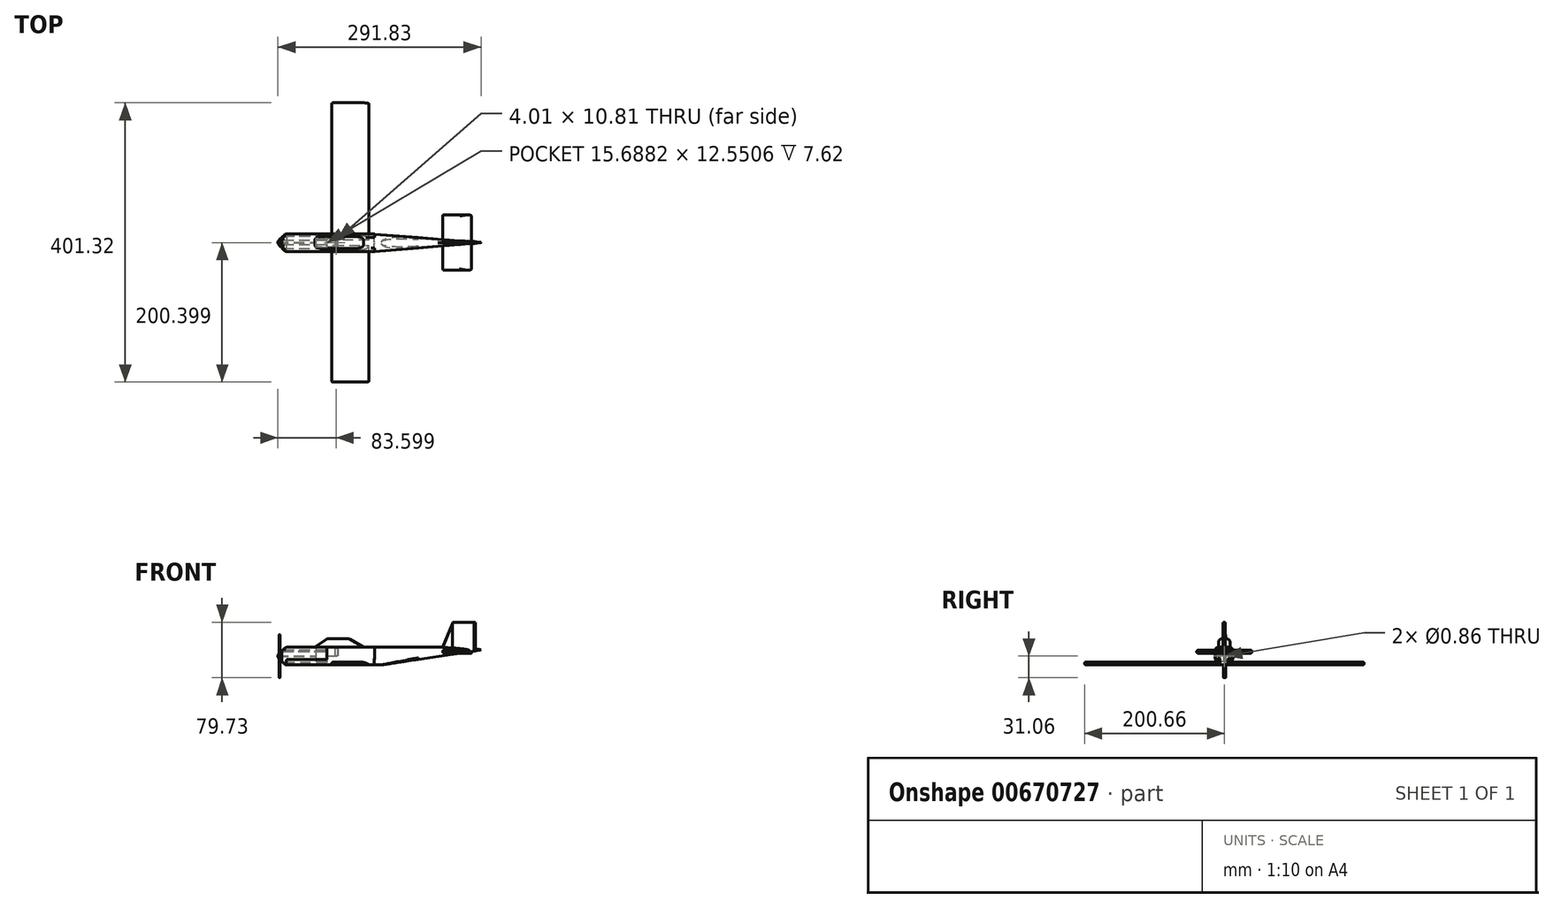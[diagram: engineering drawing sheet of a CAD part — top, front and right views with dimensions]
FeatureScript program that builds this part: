
annotation { "Feature Type Name" : "Feature", "Feature Type Description" : "" }
export const myFeature = defineFeature(function(context is Context, id is Id, definition is map)
    precondition{}
    {
        {
            var Q0;
            Q0=qCreatedBy(makeId("Top.planeOp"),FACE);
            var sketch = newSketch(context, id + "F0", { "sketchPlane" : qUnion([Q0])});
            skLineSegment(sketch, "E0.bottom", {"start": v(-64.32, 12.29) * mm, "end": v(0, 12.29) * mm});
            skLineSegment(sketch, "E0.top", {"start": v(-64.32, -13.16) * mm, "end": v(0, -13.16) * mm});
            skLineSegment(sketch, "E0.left", {"start": v(-64.32, 12.29) * mm, "end": v(-64.32, -13.16) * mm});
            skLineSegment(sketch, "E0.right", {"start": v(0, 12.29) * mm, "end": v(0, -13.16) * mm});
            skSolve(sketch);
        }
        {
            var Q0;
            Q0 = qSketchRegion(id + "F0", true);
            extrude(context, id + "F1", {"entities" : qUnion([Q0]), "endBound" : BoundingType.SYMMETRIC, "oppositeDirection" : true, "depth" : 25.4 * mm, "offsetDistance" : 25.4 * mm});
        }
        {
            var Q0;
            Q0=makeQuery(id+"F1.opExtrude","CAP_EDGE",EDGE,{"disambiguationData":[OSD([sQuery(id+"F0.wireOp",EDGE,"E0.top")])],"isStart":false});
            var Q1;
            Q1=makeQuery(id+"F1.opExtrude","CAP_EDGE",EDGE,{"disambiguationData":[OSD([sQuery(id+"F0.wireOp",EDGE,"E0.bottom")])],"isStart":false});
            fillet(context, id + "F2", {"entities" : qUnion([Q0, Q1]), "radius" : 11.65 * mm, "tangentPropagation" : true, "allowEdgeOverflow" : false});
        }
        {
            var Q0;
            Q0=makeQuery(id+"F1.opExtrude","CAP_EDGE",EDGE,{"disambiguationData":[OSD([sQuery(id+"F0.wireOp",EDGE,"E0.top")])],"isStart":true});
            var Q1;
            Q1=makeQuery(id+"F1.opExtrude","CAP_EDGE",EDGE,{"disambiguationData":[OSD([sQuery(id+"F0.wireOp",EDGE,"E0.bottom")])],"isStart":true});
            fillet(context, id + "F3", {"entities" : qUnion([Q0, Q1]), "radius" : 5.08 * mm, "tangentPropagation" : true, "allowEdgeOverflow" : false});
        }
        {
            var Q0;
            Q0=makeQuery(id+"F1.opExtrude","CAP_EDGE",EDGE,{"disambiguationData":[OSD([sQuery(id+"F0.wireOp",EDGE,"E0.left")])],"isStart":false});
            chamfer(context, id + "F4", {"entities" : qUnion([Q0]), "width" : 5.08 * mm, "tangentPropagation" : true});
        }
        {
            var Q0;
            {var subQ0=sQuery(id+"F0.wireOp",EDGE,"E0.left");Q0=makeQuery(id+"F4.opChamfer","BLEND_EDGE",EDGE,{"blendedFrom":[makeQuery(id+"F1.opExtrude","CAP_EDGE",EDGE,{"disambiguationData":[OSD([subQ0])],"isStart":true}),makeQuery(id+"F1.opExtrude","CAP_FACE",FACE,{"disambiguationData":[OSD([sQuery(id+"F0.wireOp",EDGE,"E0.bottom"),sQuery(id+"F0.wireOp",EDGE,"E0.top"),subQ0,sQuery(id+"F0.wireOp",EDGE,"E0.right")])],"isStart":true})],"blendedInto":[makeQuery(id+"F1.opExtrude","CAP_FACE",FACE,{"disambiguationData":[OSD([sQuery(id+"F0.wireOp",EDGE,"E0.bottom"),sQuery(id+"F0.wireOp",EDGE,"E0.top"),subQ0,sQuery(id+"F0.wireOp",EDGE,"E0.right")])],"isStart":true})]});}
            fillet(context, id + "F5", {"entities" : qUnion([Q0]), "radius" : 5.08 * mm, "tangentPropagation" : true, "allowEdgeOverflow" : false});
        }
        {
            var Q0;
            Q0=qCreatedBy(makeId("Right.planeOp"),FACE);
            var sketch = newSketch(context, id + "F6", { "sketchPlane" : qUnion([Q0])});
            skCircle(sketch, "E1", {"center": v(0, 0) * mm, "radius": 6.97 * mm});
            skSolve(sketch);
        }
        {
            var Q0;
            Q0 = qSketchRegion(id + "F6", true);
            extrude(context, id + "F7", {"entities" : qUnion([Q0]), "operationType" : NewBodyOperationType.ADD, "oppositeDirection" : true, "depth" : 70.1 * mm, "offsetDistance" : 25.4 * mm});
        }
        {
            var Q0;
            Q0=makeQuery(id+"F7.opExtrude","CAP_EDGE",EDGE,{"disambiguationData":[OSD([sQuery(id+"F6.wireOp",EDGE,"E1")])],"isStart":false});
            chamfer(context, id + "F8", {"entities" : qUnion([Q0]), "width" : 5.08 * mm, "tangentPropagation" : true});
        }
        {
            var Q0;
            {var subQ0=sQuery(id+"F6.wireOp",EDGE,"E1");Q0=makeQuery(id+"F8.opChamfer","BLEND_EDGE",EDGE,{"blendedFrom":[makeQuery(id+"F7.opExtrude","CAP_EDGE",EDGE,{"disambiguationData":[OSD([subQ0])],"isStart":false}),makeQuery(id+"F7.opExtrude","CAP_FACE",FACE,{"disambiguationData":[OSD([subQ0])],"isStart":false})],"blendedInto":[makeQuery(id+"F7.opExtrude","CAP_FACE",FACE,{"disambiguationData":[OSD([subQ0])],"isStart":false})]});}
            fillet(context, id + "F9", {"entities" : qUnion([Q0]), "radius" : 4.32 * mm, "tangentPropagation" : true, "allowEdgeOverflow" : false});
        }
        {
            var Q0;
            {var subQ0=sQuery(id+"F6.wireOp",EDGE,"E1");Q0=makeQuery(id+"F8.opChamfer","BLEND_EDGE",EDGE,{"blendedFrom":[makeQuery(id+"F7.opExtrude","CAP_EDGE",EDGE,{"disambiguationData":[OSD([subQ0])],"isStart":false}),makeQuery(id+"F7.opExtrude","SWEPT_FACE",FACE,{"disambiguationData":[OSD([subQ0])]})],"blendedInto":[makeQuery(id+"F7.opExtrude","SWEPT_FACE",FACE,{"disambiguationData":[OSD([subQ0])]})]});}
            fillet(context, id + "F10", {"entities" : qUnion([Q0]), "radius" : 5.08 * mm, "tangentPropagation" : true, "allowEdgeOverflow" : false});
        }
        {
            var Q0;
            Q0=qCreatedBy(makeId("Top.planeOp"),FACE);
            var sketch = newSketch(context, id + "F11", { "sketchPlane" : qUnion([Q0])});
            skLineSegment(sketch, "E2.bottom", {"start": v(-68.62, 1.8) * mm, "end": v(-67.43, 1.8) * mm});
            skLineSegment(sketch, "E2.top", {"start": v(-68.62, -1.14) * mm, "end": v(-67.43, -1.14) * mm});
            skLineSegment(sketch, "E2.left", {"start": v(-68.62, 1.8) * mm, "end": v(-68.62, -1.14) * mm});
            skLineSegment(sketch, "E2.right", {"start": v(-67.43, 1.8) * mm, "end": v(-67.43, -1.14) * mm});
            skSolve(sketch);
        }
        {
            var Q0;
            Q0 = qSketchRegion(id + "F11", true);
            extrude(context, id + "F12", {"entities" : qUnion([Q0]), "endBound" : BoundingType.SYMMETRIC, "depth" : 62.13 * mm, "offsetDistance" : 25.4 * mm});
        }
        {
            var Q0;
            {var subQ0=sQuery(id+"F11.wireOp",EDGE,"E2.left");var subQ1=sQuery(id+"F11.wireOp",EDGE,"E2.top");Q0=makeQuery(id+"F12.boolean.opBoolean","SPLIT",EDGE,{"disambiguationData":[TD([makeQuery(id+"F12.opExtrude","CAP_FACE",FACE,{"disambiguationData":[OSD([sQuery(id+"F11.wireOp",EDGE,"E2.bottom"),subQ1,subQ0,sQuery(id+"F11.wireOp",EDGE,"E2.right")])],"isStart":false})])],"derivedFrom":makeQuery(id+"F12.opExtrude","SWEPT_EDGE",EDGE,{"disambiguationData":[OSD([subQ1,subQ0])]})});}
            var Q1;
            {var subQ0=sQuery(id+"F11.wireOp",EDGE,"E2.bottom");var subQ1=sQuery(id+"F11.wireOp",EDGE,"E2.left");Q1=makeQuery(id+"F12.boolean.opBoolean","SPLIT",EDGE,{"disambiguationData":[TD([makeQuery(id+"F12.opExtrude","CAP_FACE",FACE,{"disambiguationData":[OSD([subQ0,sQuery(id+"F11.wireOp",EDGE,"E2.top"),subQ1,sQuery(id+"F11.wireOp",EDGE,"E2.right")])],"isStart":false})])],"derivedFrom":makeQuery(id+"F12.opExtrude","SWEPT_EDGE",EDGE,{"disambiguationData":[OSD([subQ0,subQ1])]})});}
            var Q2;
            {var subQ0=sQuery(id+"F11.wireOp",EDGE,"E2.bottom");var subQ1=sQuery(id+"F11.wireOp",EDGE,"E2.left");Q2=makeQuery(id+"F12.boolean.opBoolean","SPLIT",EDGE,{"disambiguationData":[TD([makeQuery(id+"F12.opExtrude","CAP_FACE",FACE,{"disambiguationData":[OSD([subQ0,sQuery(id+"F11.wireOp",EDGE,"E2.top"),subQ1,sQuery(id+"F11.wireOp",EDGE,"E2.right")])],"isStart":true})])],"derivedFrom":makeQuery(id+"F12.opExtrude","SWEPT_EDGE",EDGE,{"disambiguationData":[OSD([subQ0,subQ1])]})});}
            var Q3;
            {var subQ0=sQuery(id+"F11.wireOp",EDGE,"E2.left");var subQ1=sQuery(id+"F11.wireOp",EDGE,"E2.top");Q3=makeQuery(id+"F12.boolean.opBoolean","SPLIT",EDGE,{"disambiguationData":[TD([makeQuery(id+"F12.opExtrude","CAP_FACE",FACE,{"disambiguationData":[OSD([sQuery(id+"F11.wireOp",EDGE,"E2.bottom"),subQ1,subQ0,sQuery(id+"F11.wireOp",EDGE,"E2.right")])],"isStart":true})])],"derivedFrom":makeQuery(id+"F12.opExtrude","SWEPT_EDGE",EDGE,{"disambiguationData":[OSD([subQ1,subQ0])]})});}
            fillet(context, id + "F13", {"entities" : qUnion([Q0, Q1, Q2, Q3]), "radius" : 3.07 * mm, "tangentPropagation" : true, "allowEdgeOverflow" : false});
        }
        {
            var Q0;
            {var subQ1=sQuery(id+"F11.wireOp",EDGE,"E2.left");var subQ2=sQuery(id+"F11.wireOp",EDGE,"E2.top");var subQ3=sQuery(id+"F11.wireOp",EDGE,"E2.bottom");var subQ4=makeQuery(id+"F12.opExtrude","CAP_FACE",FACE,{"disambiguationData":[OSD([subQ3,subQ2,subQ1,sQuery(id+"F11.wireOp",EDGE,"E2.right")])],"isStart":false});Q0=makeQuery(id+"F13.opFillet","BLEND_EDGE",EDGE,{"blendedFrom":[makeQuery(id+"F12.boolean.opBoolean","SPLIT",EDGE,{"disambiguationData":[TD([subQ4])],"derivedFrom":makeQuery(id+"F12.opExtrude","SWEPT_EDGE",EDGE,{"disambiguationData":[OSD([subQ3,subQ1])]})}),makeQuery(id+"F12.boolean.opBoolean","SPLIT",EDGE,{"disambiguationData":[TD([subQ4])],"derivedFrom":makeQuery(id+"F12.opExtrude","SWEPT_EDGE",EDGE,{"disambiguationData":[OSD([subQ2,subQ1])]})})],"blendedInto":[]});}
            var Q1;
            {var subQ1=sQuery(id+"F11.wireOp",EDGE,"E2.left");var subQ2=sQuery(id+"F11.wireOp",EDGE,"E2.top");var subQ3=sQuery(id+"F11.wireOp",EDGE,"E2.bottom");var subQ4=makeQuery(id+"F12.opExtrude","CAP_FACE",FACE,{"disambiguationData":[OSD([subQ3,subQ2,subQ1,sQuery(id+"F11.wireOp",EDGE,"E2.right")])],"isStart":true});Q1=makeQuery(id+"F13.opFillet","BLEND_EDGE",EDGE,{"blendedFrom":[makeQuery(id+"F12.boolean.opBoolean","SPLIT",EDGE,{"disambiguationData":[TD([subQ4])],"derivedFrom":makeQuery(id+"F12.opExtrude","SWEPT_EDGE",EDGE,{"disambiguationData":[OSD([subQ3,subQ1])]})}),makeQuery(id+"F12.boolean.opBoolean","SPLIT",EDGE,{"disambiguationData":[TD([subQ4])],"derivedFrom":makeQuery(id+"F12.opExtrude","SWEPT_EDGE",EDGE,{"disambiguationData":[OSD([subQ2,subQ1])]})})],"blendedInto":[]});}
            fillet(context, id + "F14", {"entities" : qUnion([Q0, Q1]), "radius" : 1.47 * mm, "tangentPropagation" : true, "allowEdgeOverflow" : false});
        }
        {
            var Q0;
            Q0=makeQuery(id+"F12.opExtrude","CAP_FACE",FACE,{"disambiguationData":[OSD([sQuery(id+"F11.wireOp",EDGE,"E2.bottom"),sQuery(id+"F11.wireOp",EDGE,"E2.top"),sQuery(id+"F11.wireOp",EDGE,"E2.left"),sQuery(id+"F11.wireOp",EDGE,"E2.right")])],"isStart":false});
            var Q1;
            {var subQ0=sQuery(id+"F11.wireOp",EDGE,"E2.left");var subQ1=sQuery(id+"F11.wireOp",EDGE,"E2.top");var subQ2=sQuery(id+"F11.wireOp",EDGE,"E2.bottom");var subQ3=makeQuery(id+"F12.opExtrude","CAP_FACE",FACE,{"disambiguationData":[OSD([subQ2,subQ1,subQ0,sQuery(id+"F11.wireOp",EDGE,"E2.right")])],"isStart":true});Q1=makeQuery(id+"F14.opFillet","BLEND_EDGE",EDGE,{"blendedFrom":[makeQuery(id+"F13.opFillet","BLEND_EDGE",EDGE,{"blendedFrom":[makeQuery(id+"F12.boolean.opBoolean","SPLIT",EDGE,{"disambiguationData":[TD([subQ3])],"derivedFrom":makeQuery(id+"F12.opExtrude","SWEPT_EDGE",EDGE,{"disambiguationData":[OSD([subQ2,subQ0])]})}),makeQuery(id+"F12.boolean.opBoolean","SPLIT",EDGE,{"disambiguationData":[TD([subQ3])],"derivedFrom":makeQuery(id+"F12.opExtrude","SWEPT_EDGE",EDGE,{"disambiguationData":[OSD([subQ1,subQ0])]})})],"blendedInto":[]}),subQ3],"blendedInto":[subQ3]});}
            var Q2;
            Q2=makeQuery(id+"F12.opExtrude","CAP_EDGE",EDGE,{"disambiguationData":[OSD([sQuery(id+"F11.wireOp",EDGE,"E2.right")])],"isStart":true});
            fillet(context, id + "F15", {"entities" : qUnion([Q0, Q1, Q2]), "radius" : 0.25 * mm, "tangentPropagation" : true, "allowEdgeOverflow" : false});
        }
        {
            var Q0;
            Q0=qCreatedBy(makeId("Top.planeOp"),FACE);
            var sketch = newSketch(context, id + "F16", { "sketchPlane" : qUnion([Q0])});
            skLineSegment(sketch, "E3.bottom", {"start": v(0, 12.64) * mm, "end": v(69.03, 12.64) * mm});
            skLineSegment(sketch, "E3.top", {"start": v(0, -13.34) * mm, "end": v(69.03, -13.34) * mm});
            skLineSegment(sketch, "E3.left", {"start": v(0, 12.64) * mm, "end": v(0, -13.34) * mm});
            skLineSegment(sketch, "E3.right", {"start": v(69.03, 12.64) * mm, "end": v(69.03, -13.34) * mm});
            skSolve(sketch);
        }
        {
            var Q0;
            Q0=qCreatedBy(makeId("Top.planeOp"),FACE);
            var sketch = newSketch(context, id + "F17", { "sketchPlane" : qUnion([Q0])});
            skLineSegment(sketch, "E4.bottom", {"start": v(-15.69, 6.01) * mm, "end": v(16.04, 6.01) * mm});
            skLineSegment(sketch, "E4.top", {"start": v(-15.69, -6.54) * mm, "end": v(16.04, -6.54) * mm});
            skLineSegment(sketch, "E4.left", {"start": v(-15.69, 6.01) * mm, "end": v(-15.69, -6.54) * mm});
            skLineSegment(sketch, "E4.right", {"start": v(16.04, 6.01) * mm, "end": v(16.04, -6.54) * mm});
            skSolve(sketch);
        }
        {
            var Q0;
            Q0 = qSketchRegion(id + "F17", true);
            extrude(context, id + "F18", {"entities" : qUnion([Q0]), "operationType" : NewBodyOperationType.REMOVE, "depth" : 18.8 * mm, "offsetDistance" : 25.4 * mm});
        }
        {
            var Q0;
            Q0=makeQuery(id+"F17.imprint","IMPRINT",FACE,{"disambiguationData":[TD([[makeQuery(id+"F17.imprint","IMPRINT",EDGE,{"derivedFrom":sQuery(id+"F17.wireOp",EDGE,"E4.bottom")}),-1.0]])]});
            extrude(context, id + "F19", {"entities" : qUnion([Q0]), "operationType" : NewBodyOperationType.REMOVE, "oppositeDirection" : true, "depth" : 7.62 * mm, "offsetDistance" : 25.4 * mm});
        }
        {
            var Q0;
            Q0=makeQuery(id+"F16.imprint","IMPRINT",FACE,{"disambiguationData":[TD([[makeQuery(id+"F16.imprint","IMPRINT",EDGE,{"derivedFrom":sQuery(id+"F16.wireOp",EDGE,"E3.bottom")}),-1.0]])]});
            extrude(context, id + "F20", {"entities" : qUnion([Q0]), "operationType" : NewBodyOperationType.ADD, "endBound" : BoundingType.SYMMETRIC, "depth" : 25.4 * mm, "offsetDistance" : 25.4 * mm});
        }
        {
            var Q0;
            Q0=makeQuery(id+"F17.imprint","IMPRINT",FACE,{"disambiguationData":[TD([[makeQuery(id+"F17.imprint","IMPRINT",EDGE,{"derivedFrom":sQuery(id+"F17.wireOp",EDGE,"E4.bottom")}),-1.0]])]});
            extrude(context, id + "F21", {"entities" : qUnion([Q0]), "operationType" : NewBodyOperationType.REMOVE, "depth" : 26.16 * mm, "offsetDistance" : 25.4 * mm});
        }
        {
            var Q0;
            Q0=qCreatedBy(makeId("Top.planeOp"),FACE);
            var sketch = newSketch(context, id + "F22", { "sketchPlane" : qUnion([Q0])});
            skLineSegment(sketch, "E5.bottom", {"start": v(15.51, 5.14) * mm, "end": v(11.5, 5.14) * mm});
            skLineSegment(sketch, "E5.top", {"start": v(15.51, -5.67) * mm, "end": v(11.5, -5.67) * mm});
            skLineSegment(sketch, "E5.left", {"start": v(15.51, 5.14) * mm, "end": v(15.51, -5.67) * mm});
            skLineSegment(sketch, "E5.right", {"start": v(11.5, 5.14) * mm, "end": v(11.5, -5.67) * mm});
            skSolve(sketch);
        }
        {
            var Q0;
            Q0 = qSketchRegion(id + "F22", true);
            extrude(context, id + "F23", {"entities" : qUnion([Q0]), "depth" : 18.54 * mm, "offsetDistance" : 25.4 * mm});
        }
        {
            var Q0;
            Q0=qCreatedBy(makeId("Front.planeOp"),FACE);
            var sketch = newSketch(context, id + "F24", { "sketchPlane" : qUnion([Q0])});
            skLineSegment(sketch, "E6", {"start": v(-18.3, 11.94) * mm, "end": v(0, 24.84) * mm});
            skLineSegment(sketch, "E7", {"start": v(0, 24.84) * mm, "end": v(32.07, 24.84) * mm});
            skLineSegment(sketch, "E8", {"start": v(32.07, 24.84) * mm, "end": v(54.39, 11.94) * mm});
            skLineSegment(sketch, "E9", {"start": v(54.39, 11.94) * mm, "end": v(-18.3, 11.94) * mm});
            skSolve(sketch);
        }
        {
            var Q0;
            Q0 = qSketchRegion(id + "F24", true);
            extrude(context, id + "F25", {"entities" : qUnion([Q0]), "operationType" : NewBodyOperationType.ADD, "endBound" : BoundingType.SYMMETRIC, "depth" : 16.76 * mm, "offsetDistance" : 25.4 * mm});
        }
        {
            var Q0;
            Q0=makeQuery(id+"F25.opExtrude","CAP_EDGE",EDGE,{"disambiguationData":[OSD([sQuery(id+"F24.wireOp",EDGE,"E7")])],"isStart":false});
            var Q1;
            Q1=makeQuery(id+"F25.opExtrude","CAP_EDGE",EDGE,{"disambiguationData":[OSD([sQuery(id+"F24.wireOp",EDGE,"E7")])],"isStart":true});
            var Q2;
            Q2=makeQuery(id+"F25.opExtrude","CAP_EDGE",EDGE,{"disambiguationData":[OSD([sQuery(id+"F24.wireOp",EDGE,"E6")])],"isStart":false});
            var Q3;
            Q3=makeQuery(id+"F25.opExtrude","CAP_EDGE",EDGE,{"disambiguationData":[OSD([sQuery(id+"F24.wireOp",EDGE,"E6")])],"isStart":true});
            var Q4;
            Q4=makeQuery(id+"F25.opExtrude","CAP_EDGE",EDGE,{"disambiguationData":[OSD([sQuery(id+"F24.wireOp",EDGE,"E8")])],"isStart":false});
            var Q5;
            Q5=makeQuery(id+"F25.opExtrude","CAP_EDGE",EDGE,{"disambiguationData":[OSD([sQuery(id+"F24.wireOp",EDGE,"E8")])],"isStart":true});
            var Q6;
            Q6=makeQuery(id+"F25.opExtrude","SWEPT_EDGE",EDGE,{"disambiguationData":[OSD([sQuery(id+"F24.wireOp",EDGE,"E7"),sQuery(id+"F24.wireOp",EDGE,"E8")])]});
            var Q7;
            Q7=makeQuery(id+"F25.opExtrude","SWEPT_EDGE",EDGE,{"disambiguationData":[OSD([sQuery(id+"F24.wireOp",EDGE,"E6"),sQuery(id+"F24.wireOp",EDGE,"E7")])]});
            fillet(context, id + "F26", {"entities" : qUnion([Q0, Q1, Q2, Q3, Q4, Q5, Q6, Q7]), "radius" : 5.08 * mm, "tangentPropagation" : true, "allowEdgeOverflow" : false});
        }
        {
            var Q0;
            Q0=makeQuery(id+"F20.opExtrude","CAP_EDGE",EDGE,{"disambiguationData":[OSD([sQuery(id+"F16.wireOp",EDGE,"E3.top")])],"isStart":true});
            var Q1;
            Q1=makeQuery(id+"F20.opExtrude","CAP_EDGE",EDGE,{"disambiguationData":[OSD([sQuery(id+"F16.wireOp",EDGE,"E3.bottom")])],"isStart":true});
            fillet(context, id + "F27", {"entities" : qUnion([Q0, Q1]), "radius" : 12.26 * mm, "tangentPropagation" : true, "allowEdgeOverflow" : false});
        }
        {
            var Q0;
            Q0=makeQuery(id+"F20.opExtrude","CAP_EDGE",EDGE,{"disambiguationData":[OSD([sQuery(id+"F16.wireOp",EDGE,"E3.bottom")])],"isStart":false});
            var Q1;
            Q1=makeQuery(id+"F20.opExtrude","CAP_EDGE",EDGE,{"disambiguationData":[OSD([sQuery(id+"F16.wireOp",EDGE,"E3.top")])],"isStart":false});
            fillet(context, id + "F28", {"entities" : qUnion([Q0, Q1]), "radius" : 5.08 * mm, "tangentPropagation" : true, "allowEdgeOverflow" : false});
        }
        {
            var Q0;
            Q0=qCreatedBy(makeId("Top.planeOp"),FACE);
            var sketch = newSketch(context, id + "F29", { "sketchPlane" : qUnion([Q0])});
            skLineSegment(sketch, "E10", {"start": v(67.95, -12.97) * mm, "end": v(224.25, 0) * mm});
            skLineSegment(sketch, "E11", {"start": v(224.25, 0) * mm, "end": v(68.26, 11.72) * mm});
            skLineSegment(sketch, "E12", {"start": v(68.26, 11.72) * mm, "end": v(67.95, -12.97) * mm});
            skSolve(sketch);
        }
        {
            var Q0;
            Q0 = qSketchRegion(id + "F29", true);
            extrude(context, id + "F30", {"entities" : qUnion([Q0]), "operationType" : NewBodyOperationType.ADD, "endBound" : BoundingType.SYMMETRIC, "depth" : 25.4 * mm, "offsetDistance" : 25.4 * mm});
        }
        {
            var Q0;
            Q0=qCreatedBy(makeId("Front.planeOp"),FACE);
            var sketch = newSketch(context, id + "F31", { "sketchPlane" : qUnion([Q0])});
            skLineSegment(sketch, "E13", {"start": v(72.32, -13.6) * mm, "end": v(239.57, 11.72) * mm});
            skLineSegment(sketch, "E14", {"start": v(239.57, 11.72) * mm, "end": v(239.57, -12.97) * mm});
            skLineSegment(sketch, "E15", {"start": v(239.57, -12.97) * mm, "end": v(72.32, -13.6) * mm});
            skSolve(sketch);
        }
        {
            var Q0;
            Q0 = qSketchRegion(id + "F31", true);
            extrude(context, id + "F32", {"entities" : qUnion([Q0]), "operationType" : NewBodyOperationType.REMOVE, "endBound" : BoundingType.SYMMETRIC, "oppositeDirection" : true, "depth" : 25.4 * mm, "offsetDistance" : 25.4 * mm});
        }
        {
            var Q0;
            Q0=makeQuery(id+"F30.opExtrude","CAP_EDGE",EDGE,{"disambiguationData":[OSD([sQuery(id+"F29.wireOp",EDGE,"E10")])],"isStart":false});
            var Q1;
            Q1=makeQuery(id+"F30.opExtrude","CAP_EDGE",EDGE,{"disambiguationData":[OSD([sQuery(id+"F29.wireOp",EDGE,"E11")])],"isStart":false});
            fillet(context, id + "F33", {"entities" : qUnion([Q0, Q1]), "radius" : 5.08 * mm, "tangentPropagation" : true, "allowEdgeOverflow" : false});
        }
        {
            var Q0;
            Q0=makeQuery(id+"F30.opExtrude","CAP_EDGE",EDGE,{"disambiguationData":[OSD([sQuery(id+"F29.wireOp",EDGE,"E11")])],"isStart":true});
            var Q1;
            Q1=makeQuery(id+"F30.opExtrude","CAP_EDGE",EDGE,{"disambiguationData":[OSD([sQuery(id+"F29.wireOp",EDGE,"E10")])],"isStart":true});
            fillet(context, id + "F34", {"entities" : qUnion([Q0, Q1]), "radius" : 10.42 * mm, "tangentPropagation" : true, "allowEdgeOverflow" : false});
        }
        {
            var Q0;
            Q0=qCreatedBy(makeId("Top.planeOp"),FACE);
            var sketch = newSketch(context, id + "F35", { "sketchPlane" : qUnion([Q0])});
            skLineSegment(sketch, "E16.bottom", {"start": v(213.5, 1.58) * mm, "end": v(181.72, 1.58) * mm});
            skLineSegment(sketch, "E16.top", {"start": v(213.5, -1.58) * mm, "end": v(181.72, -1.58) * mm});
            skLineSegment(sketch, "E16.left", {"start": v(213.5, 1.58) * mm, "end": v(213.5, -1.58) * mm});
            skLineSegment(sketch, "E16.right", {"start": v(181.72, 1.58) * mm, "end": v(181.72, -1.58) * mm});
            skPoint(sketch, "E16.middle", {"position": v(197.61, 0) * mm});
            skSolve(sketch);
        }
        {
            var Q0;
            Q0 = qSketchRegion(id + "F35", true);
            extrude(context, id + "F36", {"entities" : qUnion([Q0]), "operationType" : NewBodyOperationType.ADD, "depth" : 48.5 * mm, "offsetDistance" : 25.4 * mm});
        }
        {
            var Q0;
            Q0=qCreatedBy(makeId("Front.planeOp"),FACE);
            var sketch = newSketch(context, id + "F37", { "sketchPlane" : qUnion([Q0])});
            skLineSegment(sketch, "E17", {"start": v(180.48, 2.56) * mm, "end": v(214.75, 7.76) * mm});
            skLineSegment(sketch, "E18", {"start": v(214.75, 7.76) * mm, "end": v(213.42, -1.75) * mm});
            skLineSegment(sketch, "E19", {"start": v(213.42, -1.75) * mm, "end": v(180.7, -1.75) * mm});
            skLineSegment(sketch, "E20", {"start": v(180.7, -1.75) * mm, "end": v(180.48, 2.56) * mm});
            skSolve(sketch);
        }
        {
            var Q0;
            Q0 = qSketchRegion(id + "F37", true);
            extrude(context, id + "F38", {"entities" : qUnion([Q0]), "operationType" : NewBodyOperationType.REMOVE, "endBound" : BoundingType.SYMMETRIC, "oppositeDirection" : true, "depth" : 25.4 * mm, "offsetDistance" : 25.4 * mm});
        }
        {
            var Q0;
            Q0=qCreatedBy(makeId("Front.planeOp"),FACE);
            var sketch = newSketch(context, id + "F39", { "sketchPlane" : qUnion([Q0])});
            skLineSegment(sketch, "E21", {"start": v(165.76, 11.4) * mm, "end": v(181.72, 48.86) * mm});
            skLineSegment(sketch, "E22", {"start": v(181.72, 48.86) * mm, "end": v(181.72, 12.33) * mm});
            skLineSegment(sketch, "E23", {"start": v(181.72, 12.33) * mm, "end": v(165.76, 11.4) * mm});
            skSolve(sketch);
        }
        {
            var Q0;
            Q0 = qSketchRegion(id + "F39", true);
            extrude(context, id + "F40", {"entities" : qUnion([Q0]), "operationType" : NewBodyOperationType.ADD, "endBound" : BoundingType.SYMMETRIC, "depth" : 3.2 * mm, "offsetDistance" : 25.4 * mm});
        }
        {
            var Q0;
            Q0 = qSketchRegion(id + "F39", true);
            extrude(context, id + "F41", {"entities" : qUnion([Q0]), "operationType" : NewBodyOperationType.ADD, "endBound" : BoundingType.SYMMETRIC, "oppositeDirection" : true, "depth" : 3.15 * mm, "offsetDistance" : 25.4 * mm});
        }
        {
            var Q0;
            Q0=qCreatedBy(makeId("Right.planeOp"),FACE);
            var sketch = newSketch(context, id + "F42", { "sketchPlane" : qUnion([Q0])});
            skLineSegment(sketch, "E24.bottom", {"start": v(9.21, 9.39) * mm, "end": v(3.59, 9.39) * mm});
            skLineSegment(sketch, "E24.top", {"start": v(9.21, 6.69) * mm, "end": v(3.59, 6.69) * mm});
            skLineSegment(sketch, "E24.left", {"start": v(9.21, 9.39) * mm, "end": v(9.21, 6.69) * mm});
            skLineSegment(sketch, "E24.right", {"start": v(3.59, 9.39) * mm, "end": v(3.59, 6.69) * mm});
            skLineSegment(sketch, "E25.bottom", {"start": v(-2.69, 9.34) * mm, "end": v(-8.61, 9.34) * mm});
            skLineSegment(sketch, "E25.top", {"start": v(-2.69, 7) * mm, "end": v(-8.61, 7) * mm});
            skLineSegment(sketch, "E25.left", {"start": v(-2.69, 9.34) * mm, "end": v(-2.69, 7) * mm});
            skLineSegment(sketch, "E25.right", {"start": v(-8.61, 9.34) * mm, "end": v(-8.61, 7) * mm});
            skSolve(sketch);
        }
        {
            var Q0;
            Q0 = qSketchRegion(id + "F42", true);
            extrude(context, id + "F43", {"entities" : qUnion([Q0]), "operationType" : NewBodyOperationType.REMOVE, "oppositeDirection" : true, "depth" : 66.3 * mm, "offsetDistance" : 25.4 * mm});
        }
        {
            var Q0;
            Q0=qCreatedBy(makeId("Right.planeOp"),FACE);
            var sketch = newSketch(context, id + "F44", { "sketchPlane" : qUnion([Q0])});
            skLineSegment(sketch, "E26.bottom", {"start": v(9.2, 9.38) * mm, "end": v(3.56, 9.38) * mm});
            skLineSegment(sketch, "E26.top", {"start": v(9.2, 6.75) * mm, "end": v(3.56, 6.75) * mm});
            skLineSegment(sketch, "E26.left", {"start": v(9.2, 9.38) * mm, "end": v(9.2, 6.75) * mm});
            skLineSegment(sketch, "E26.right", {"start": v(3.56, 9.38) * mm, "end": v(3.56, 6.75) * mm});
            skLineSegment(sketch, "E27.bottom", {"start": v(-2.65, 9.18) * mm, "end": v(-8.57, 9.18) * mm});
            skLineSegment(sketch, "E27.top", {"start": v(-2.65, 7.03) * mm, "end": v(-8.57, 7.03) * mm});
            skLineSegment(sketch, "E27.left", {"start": v(-2.65, 9.18) * mm, "end": v(-2.65, 7.03) * mm});
            skLineSegment(sketch, "E27.right", {"start": v(-8.57, 9.18) * mm, "end": v(-8.57, 7.03) * mm});
            skSolve(sketch);
        }
        {
            var Q0;
            Q0 = qSketchRegion(id + "F44", true);
            extrude(context, id + "F45", {"entities" : qUnion([Q0]), "oppositeDirection" : true, "depth" : 62.6 * mm, "offsetDistance" : 25.4 * mm});
        }
        {
            var Q0;
            Q0=qCreatedBy(makeId("Front.planeOp"),FACE);
            var sketch = newSketch(context, id + "F46", { "sketchPlane" : qUnion([Q0])});
            skLineSegment(sketch, "E28.bottom", {"start": v(166.62, 8.4) * mm, "end": v(207.88, 8.4) * mm});
            skLineSegment(sketch, "E28.top", {"start": v(166.62, 4.4) * mm, "end": v(207.88, 4.4) * mm});
            skLineSegment(sketch, "E28.left", {"start": v(166.62, 8.4) * mm, "end": v(166.62, 4.4) * mm});
            skLineSegment(sketch, "E28.right", {"start": v(207.88, 8.4) * mm, "end": v(207.88, 4.4) * mm});
            skSolve(sketch);
        }
        {
            var Q0;
            Q0=qCreatedBy(makeId("Front.planeOp"),FACE);
            var sketch = newSketch(context, id + "F47", { "sketchPlane" : qUnion([Q0])});
            skLineSegment(sketch, "E29.bottom", {"start": v(6.95, -8.4) * mm, "end": v(60.8, -8.4) * mm});
            skLineSegment(sketch, "E29.top", {"start": v(6.95, -12.35) * mm, "end": v(60.8, -12.35) * mm});
            skLineSegment(sketch, "E29.left", {"start": v(6.95, -8.4) * mm, "end": v(6.95, -12.35) * mm});
            skLineSegment(sketch, "E29.right", {"start": v(60.8, -8.4) * mm, "end": v(60.8, -12.35) * mm});
            skSolve(sketch);
        }
        {
            var Q0;
            Q0 = qSketchRegion(id + "F47", true);
            extrude(context, id + "F48", {"entities" : qUnion([Q0]), "operationType" : NewBodyOperationType.ADD, "endBound" : BoundingType.SYMMETRIC, "depth" : 401.32 * mm, "offsetDistance" : 25.4 * mm});
        }
        {
            var Q0;
            {var subQ0=sQuery(id+"F47.wireOp",EDGE,"E29.bottom");var subQ1=sQuery(id+"F47.wireOp",EDGE,"E29.left");Q0=makeQuery(id+"F48.boolean.opBoolean","SPLIT",EDGE,{"disambiguationData":[TD([makeQuery(id+"F27.opFillet","BLEND_FACE",FACE,{"disambiguationData":[OSD([sQuery(id+"F16.wireOp",EDGE,"E3.bottom")])]})])],"derivedFrom":makeQuery(id+"F48.opExtrude","SWEPT_EDGE",EDGE,{"disambiguationData":[OSD([subQ0,subQ1])]})});}
            var Q1;
            {var subQ0=sQuery(id+"F47.wireOp",EDGE,"E29.top");var subQ1=sQuery(id+"F47.wireOp",EDGE,"E29.left");Q1=makeQuery(id+"F48.boolean.opBoolean","SPLIT",EDGE,{"disambiguationData":[TD([makeQuery(id+"F27.opFillet","BLEND_FACE",FACE,{"disambiguationData":[OSD([sQuery(id+"F16.wireOp",EDGE,"E3.bottom")])]})])],"derivedFrom":makeQuery(id+"F48.opExtrude","SWEPT_EDGE",EDGE,{"disambiguationData":[OSD([subQ0,subQ1])]})});}
            var Q2;
            {var subQ0=sQuery(id+"F47.wireOp",EDGE,"E29.left");var subQ1=sQuery(id+"F47.wireOp",EDGE,"E29.top");Q2=makeQuery(id+"F48.boolean.opBoolean","SPLIT",EDGE,{"disambiguationData":[TD([makeQuery(id+"F27.opFillet","BLEND_FACE",FACE,{"disambiguationData":[OSD([sQuery(id+"F16.wireOp",EDGE,"E3.top")])]})])],"derivedFrom":makeQuery(id+"F48.opExtrude","SWEPT_EDGE",EDGE,{"disambiguationData":[OSD([subQ1,subQ0])]})});}
            var Q3;
            {var subQ0=sQuery(id+"F47.wireOp",EDGE,"E29.left");var subQ1=sQuery(id+"F47.wireOp",EDGE,"E29.bottom");Q3=makeQuery(id+"F48.boolean.opBoolean","SPLIT",EDGE,{"disambiguationData":[TD([makeQuery(id+"F27.opFillet","BLEND_FACE",FACE,{"disambiguationData":[OSD([sQuery(id+"F16.wireOp",EDGE,"E3.top")])]})])],"derivedFrom":makeQuery(id+"F48.opExtrude","SWEPT_EDGE",EDGE,{"disambiguationData":[OSD([subQ1,subQ0])]})});}
            fillet(context, id + "F49", {"entities" : qUnion([Q0, Q1, Q2, Q3]), "radius" : 2.88 * mm, "tangentPropagation" : true, "allowEdgeOverflow" : false});
        }
        {
            var Q0;
            {var subQ0=sQuery(id+"F47.wireOp",EDGE,"E29.bottom");var subQ1=sQuery(id+"F47.wireOp",EDGE,"E29.right");Q0=makeQuery(id+"F48.boolean.opBoolean","SPLIT",EDGE,{"disambiguationData":[TD([makeQuery(id+"F27.opFillet","BLEND_FACE",FACE,{"disambiguationData":[OSD([sQuery(id+"F16.wireOp",EDGE,"E3.top")])]})])],"derivedFrom":makeQuery(id+"F48.opExtrude","SWEPT_EDGE",EDGE,{"disambiguationData":[OSD([subQ0,subQ1])]})});}
            var Q1;
            {var subQ0=sQuery(id+"F47.wireOp",EDGE,"E29.bottom");var subQ1=sQuery(id+"F47.wireOp",EDGE,"E29.right");Q1=makeQuery(id+"F48.boolean.opBoolean","SPLIT",EDGE,{"disambiguationData":[TD([makeQuery(id+"F27.opFillet","BLEND_FACE",FACE,{"disambiguationData":[OSD([sQuery(id+"F16.wireOp",EDGE,"E3.bottom")])]})])],"derivedFrom":makeQuery(id+"F48.opExtrude","SWEPT_EDGE",EDGE,{"disambiguationData":[OSD([subQ0,subQ1])]})});}
            fillet(context, id + "F50", {"entities" : qUnion([Q0, Q1]), "radius" : 22.7 * mm, "tangentPropagation" : true, "allowEdgeOverflow" : false});
        }
        {
            var Q0;
            Q0=makeQuery(id+"F48.opExtrude","CAP_FACE",FACE,{"disambiguationData":[OSD([sQuery(id+"F47.wireOp",EDGE,"E29.bottom"),sQuery(id+"F47.wireOp",EDGE,"E29.top"),sQuery(id+"F47.wireOp",EDGE,"E29.left"),sQuery(id+"F47.wireOp",EDGE,"E29.right")])],"isStart":false});
            var Q1;
            Q1=makeQuery(id+"F48.opExtrude","CAP_FACE",FACE,{"disambiguationData":[OSD([sQuery(id+"F47.wireOp",EDGE,"E29.bottom"),sQuery(id+"F47.wireOp",EDGE,"E29.top"),sQuery(id+"F47.wireOp",EDGE,"E29.left"),sQuery(id+"F47.wireOp",EDGE,"E29.right")])],"isStart":true});
            fillet(context, id + "F51", {"entities" : qUnion([Q0, Q1]), "radius" : 1.66 * mm, "tangentPropagation" : true, "allowEdgeOverflow" : false});
        }
        {
            var Q0;
            Q0 = qSketchRegion(id + "F46", true);
            extrude(context, id + "F52", {"entities" : qUnion([Q0]), "operationType" : NewBodyOperationType.ADD, "endBound" : BoundingType.SYMMETRIC, "depth" : 79.25 * mm, "offsetDistance" : 25.4 * mm});
        }
        {
            var Q0;
            {var subQ0=sQuery(id+"F46.wireOp",EDGE,"E28.bottom");var subQ1=sQuery(id+"F46.wireOp",EDGE,"E28.left");Q0=makeQuery(id+"F52.boolean.opBoolean","SPLIT",EDGE,{"disambiguationData":[TD([makeQuery(id+"F33.opFillet","BLEND_FACE",FACE,{"disambiguationData":[OSD([sQuery(id+"F29.wireOp",EDGE,"E10")])]})])],"derivedFrom":makeQuery(id+"F52.opExtrude","SWEPT_EDGE",EDGE,{"disambiguationData":[OSD([subQ0,subQ1])]})});}
            var Q1;
            {var subQ0=sQuery(id+"F46.wireOp",EDGE,"E28.left");var subQ1=sQuery(id+"F46.wireOp",EDGE,"E28.top");Q1=makeQuery(id+"F52.boolean.opBoolean","SPLIT",EDGE,{"disambiguationData":[TD([makeQuery(id+"F30.opExtrude","SWEPT_FACE",FACE,{"disambiguationData":[OSD([sQuery(id+"F29.wireOp",EDGE,"E10")])]})])],"derivedFrom":makeQuery(id+"F52.opExtrude","SWEPT_EDGE",EDGE,{"disambiguationData":[OSD([subQ1,subQ0])]})});}
            var Q2;
            {var subQ0=sQuery(id+"F46.wireOp",EDGE,"E28.left");var subQ1=sQuery(id+"F46.wireOp",EDGE,"E28.top");Q2=makeQuery(id+"F52.boolean.opBoolean","SPLIT",EDGE,{"disambiguationData":[TD([makeQuery(id+"F30.opExtrude","SWEPT_FACE",FACE,{"disambiguationData":[OSD([sQuery(id+"F29.wireOp",EDGE,"E11")])]})])],"derivedFrom":makeQuery(id+"F52.opExtrude","SWEPT_EDGE",EDGE,{"disambiguationData":[OSD([subQ1,subQ0])]})});}
            var Q3;
            {var subQ0=sQuery(id+"F46.wireOp",EDGE,"E28.left");var subQ1=sQuery(id+"F46.wireOp",EDGE,"E28.bottom");Q3=makeQuery(id+"F52.boolean.opBoolean","SPLIT",EDGE,{"disambiguationData":[TD([makeQuery(id+"F33.opFillet","BLEND_FACE",FACE,{"disambiguationData":[OSD([sQuery(id+"F29.wireOp",EDGE,"E11")])]})])],"derivedFrom":makeQuery(id+"F52.opExtrude","SWEPT_EDGE",EDGE,{"disambiguationData":[OSD([subQ1,subQ0])]})});}
            fillet(context, id + "F53", {"entities" : qUnion([Q0, Q1, Q2, Q3]), "radius" : 1.84 * mm, "tangentPropagation" : true, "allowEdgeOverflow" : false});
        }
        {
            var Q0;
            Q0=makeQuery(id+"F40.opExtrude","SWEPT_EDGE",EDGE,{"disambiguationData":[OSD([sQuery(id+"F39.wireOp",EDGE,"E21"),sQuery(id+"F39.wireOp",EDGE,"E22")])]});
            fillet(context, id + "F54", {"entities" : qUnion([Q0]), "radius" : 0.05 * mm, "tangentPropagation" : true, "allowEdgeOverflow" : false});
        }
        {
            var Q0;
            Q0=makeQuery(id+"F52.opExtrude","CAP_FACE",FACE,{"disambiguationData":[OSD([sQuery(id+"F46.wireOp",EDGE,"E28.bottom"),sQuery(id+"F46.wireOp",EDGE,"E28.top"),sQuery(id+"F46.wireOp",EDGE,"E28.left"),sQuery(id+"F46.wireOp",EDGE,"E28.right")])],"isStart":false});
            var Q1;
            Q1=makeQuery(id+"F52.opExtrude","CAP_FACE",FACE,{"disambiguationData":[OSD([sQuery(id+"F46.wireOp",EDGE,"E28.bottom"),sQuery(id+"F46.wireOp",EDGE,"E28.top"),sQuery(id+"F46.wireOp",EDGE,"E28.left"),sQuery(id+"F46.wireOp",EDGE,"E28.right")])],"isStart":true});
            fillet(context, id + "F55", {"entities" : qUnion([Q0, Q1]), "radius" : 1.66 * mm, "tangentPropagation" : true, "allowEdgeOverflow" : false});
        }
        {
            var Q0;
            Q0=qCreatedBy(makeId("Right.planeOp"),FACE);
            var sketch = newSketch(context, id + "F56", { "sketchPlane" : qUnion([Q0])});
            skCircle(sketch, "E30", {"center": v(0, 0) * mm, "radius": 0.43 * mm});
            skSolve(sketch);
        }
        {
            var Q0;
            Q0 = qSketchRegion(id + "F56", true);
            extrude(context, id + "F57", {"entities" : qUnion([Q0]), "operationType" : NewBodyOperationType.REMOVE, "oppositeDirection" : true, "depth" : 147.32 * mm, "offsetDistance" : 25.4 * mm});
        }
        {
            var Q0;
            Q0=sQuery(id+"F56.wireOp",EDGE,"E30");
            extrude(context, id + "F58", {"bodyType" : ToolBodyType.SURFACE, "surfaceEntities" : qUnion([Q0]), "oppositeDirection" : true, "depth" : 72.42 * mm, "offsetDistance" : 25.4 * mm});
        }
        {
            var Q0;
            Q0=makeQuery(id+"F40.opExtrude","CAP_EDGE",EDGE,{"disambiguationData":[OSD([sQuery(id+"F39.wireOp",EDGE,"E21")])],"isStart":false});
            var Q1;
            Q1=makeQuery(id+"F40.opExtrude","CAP_EDGE",EDGE,{"disambiguationData":[OSD([sQuery(id+"F39.wireOp",EDGE,"E21")])],"isStart":true});
            fillet(context, id + "F59", {"entities" : qUnion([Q0, Q1]), "radius" : 1.27 * mm, "tangentPropagation" : true, "allowEdgeOverflow" : false});
        }
        {
            var Q0;
            Q0=qCreatedBy(makeId("Front.planeOp"),FACE);
            var sketch = newSketch(context, id + "F60", { "sketchPlane" : qUnion([Q0])});
            skLineSegment(sketch, "E31", {"start": v(180.07, 45.35) * mm, "end": v(181.65, 49.03) * mm});
            skLineSegment(sketch, "E32", {"start": v(181.65, 49.03) * mm, "end": v(179.14, 49.03) * mm});
            skLineSegment(sketch, "E33", {"start": v(179.14, 49.03) * mm, "end": v(180.07, 45.35) * mm});
            skSolve(sketch);
        }
        {
            var Q0;
            Q0 = qSketchRegion(id + "F60", true);
            extrude(context, id + "F61", {"entities" : qUnion([Q0]), "operationType" : NewBodyOperationType.REMOVE, "endBound" : BoundingType.SYMMETRIC, "oppositeDirection" : true, "depth" : 25.4 * mm, "offsetDistance" : 25.4 * mm});
        }
        {
            var Q0;
            Q0=makeQuery(id+"F36.opExtrude","SWEPT_EDGE",EDGE,{"disambiguationData":[OSD([sQuery(id+"F35.wireOp",EDGE,"E16.bottom"),sQuery(id+"F35.wireOp",EDGE,"E16.left")])]});
            var Q1;
            Q1=makeQuery(id+"F36.opExtrude","SWEPT_EDGE",EDGE,{"disambiguationData":[OSD([sQuery(id+"F35.wireOp",EDGE,"E16.top"),sQuery(id+"F35.wireOp",EDGE,"E16.left")])]});
            chamfer(context, id + "F62", {"entities" : qUnion([Q0, Q1]), "width" : 1.52 * mm, "tangentPropagation" : true});
        }
        {
            var Q0;
            {var subQ1=sQuery(id+"F35.wireOp",EDGE,"E16.left");var subQ2=sQuery(id+"F35.wireOp",EDGE,"E16.top");Q0=makeQuery(id+"F62.opChamfer","BLEND_EDGE",EDGE,{"blendedFrom":[makeQuery(id+"F36.opExtrude","SWEPT_EDGE",EDGE,{"disambiguationData":[OSD([subQ2,subQ1])]}),makeQuery(id+"F52.boolean.opBoolean","SPLIT",FACE,{"disambiguationData":[TD([makeQuery(id+"F33.opFillet","BLEND_FACE",FACE,{"disambiguationData":[OSD([sQuery(id+"F29.wireOp",EDGE,"E10")])]})])],"derivedFrom":makeQuery(id+"F36.opExtrude","SWEPT_FACE",FACE,{"disambiguationData":[OSD([subQ2])]})})],"blendedInto":[makeQuery(id+"F52.boolean.opBoolean","SPLIT",FACE,{"disambiguationData":[TD([makeQuery(id+"F33.opFillet","BLEND_FACE",FACE,{"disambiguationData":[OSD([sQuery(id+"F29.wireOp",EDGE,"E10")])]})])],"derivedFrom":makeQuery(id+"F36.opExtrude","SWEPT_FACE",FACE,{"disambiguationData":[OSD([subQ2])]})})]});}
            var Q1;
            {var subQ1=sQuery(id+"F35.wireOp",EDGE,"E16.left");var subQ2=sQuery(id+"F35.wireOp",EDGE,"E16.bottom");Q1=makeQuery(id+"F62.opChamfer","BLEND_EDGE",EDGE,{"blendedFrom":[makeQuery(id+"F36.opExtrude","SWEPT_EDGE",EDGE,{"disambiguationData":[OSD([subQ2,subQ1])]}),makeQuery(id+"F52.boolean.opBoolean","SPLIT",FACE,{"disambiguationData":[TD([makeQuery(id+"F33.opFillet","BLEND_FACE",FACE,{"disambiguationData":[OSD([sQuery(id+"F29.wireOp",EDGE,"E11")])]})])],"derivedFrom":makeQuery(id+"F36.opExtrude","SWEPT_FACE",FACE,{"disambiguationData":[OSD([subQ2])]})})],"blendedInto":[makeQuery(id+"F52.boolean.opBoolean","SPLIT",FACE,{"disambiguationData":[TD([makeQuery(id+"F33.opFillet","BLEND_FACE",FACE,{"disambiguationData":[OSD([sQuery(id+"F29.wireOp",EDGE,"E11")])]})])],"derivedFrom":makeQuery(id+"F36.opExtrude","SWEPT_FACE",FACE,{"disambiguationData":[OSD([subQ2])]})})]});}
            chamfer(context, id + "F63", {"entities" : qUnion([Q0, Q1]), "width" : 0.5 * mm, "tangentPropagation" : true});
        }
        {
            var Q0;
            {var subQ1=sQuery(id+"F35.wireOp",EDGE,"E16.left");var subQ2=sQuery(id+"F35.wireOp",EDGE,"E16.bottom");var subQ3=makeQuery(id+"F52.boolean.opBoolean","SPLIT",FACE,{"disambiguationData":[TD([makeQuery(id+"F33.opFillet","BLEND_FACE",FACE,{"disambiguationData":[OSD([sQuery(id+"F29.wireOp",EDGE,"E11")])]})])],"derivedFrom":makeQuery(id+"F36.opExtrude","SWEPT_FACE",FACE,{"disambiguationData":[OSD([subQ2])]})});Q0=makeQuery(id+"F63.opChamfer","BLEND_EDGE",EDGE,{"blendedFrom":[makeQuery(id+"F62.opChamfer","BLEND_EDGE",EDGE,{"blendedFrom":[makeQuery(id+"F36.opExtrude","SWEPT_EDGE",EDGE,{"disambiguationData":[OSD([subQ2,subQ1])]}),subQ3],"blendedInto":[subQ3]}),subQ3],"blendedInto":[subQ3]});}
            var Q1;
            {var subQ1=sQuery(id+"F35.wireOp",EDGE,"E16.left");var subQ2=sQuery(id+"F35.wireOp",EDGE,"E16.top");var subQ3=makeQuery(id+"F52.boolean.opBoolean","SPLIT",FACE,{"disambiguationData":[TD([makeQuery(id+"F33.opFillet","BLEND_FACE",FACE,{"disambiguationData":[OSD([sQuery(id+"F29.wireOp",EDGE,"E10")])]})])],"derivedFrom":makeQuery(id+"F36.opExtrude","SWEPT_FACE",FACE,{"disambiguationData":[OSD([subQ2])]})});Q1=makeQuery(id+"F63.opChamfer","BLEND_EDGE",EDGE,{"blendedFrom":[makeQuery(id+"F62.opChamfer","BLEND_EDGE",EDGE,{"blendedFrom":[makeQuery(id+"F36.opExtrude","SWEPT_EDGE",EDGE,{"disambiguationData":[OSD([subQ2,subQ1])]}),subQ3],"blendedInto":[subQ3]}),subQ3],"blendedInto":[subQ3]});}
            chamfer(context, id + "F64", {"entities" : qUnion([Q0, Q1]), "width" : 0.18 * mm, "tangentPropagation" : true});
        }
        {
            var Q0;
            {var subQ0=sQuery(id+"F46.wireOp",EDGE,"E28.right");var subQ1=sQuery(id+"F46.wireOp",EDGE,"E28.bottom");Q0=makeQuery(id+"F52.boolean.opBoolean","SPLIT",EDGE,{"disambiguationData":[TD([makeQuery(id+"F36.opExtrude","SWEPT_FACE",FACE,{"disambiguationData":[OSD([sQuery(id+"F35.wireOp",EDGE,"E16.top")])]})])],"derivedFrom":makeQuery(id+"F52.opExtrude","SWEPT_EDGE",EDGE,{"disambiguationData":[OSD([subQ1,subQ0])]})});}
            var Q1;
            {var subQ0=sQuery(id+"F46.wireOp",EDGE,"E28.bottom");var subQ1=sQuery(id+"F46.wireOp",EDGE,"E28.right");Q1=makeQuery(id+"F52.boolean.opBoolean","SPLIT",EDGE,{"disambiguationData":[TD([makeQuery(id+"F36.opExtrude","SWEPT_FACE",FACE,{"disambiguationData":[OSD([sQuery(id+"F35.wireOp",EDGE,"E16.bottom")])]})])],"derivedFrom":makeQuery(id+"F52.opExtrude","SWEPT_EDGE",EDGE,{"disambiguationData":[OSD([subQ0,subQ1])]})});}
            fillet(context, id + "F65", {"entities" : qUnion([Q0, Q1]), "radius" : 38.57 * mm, "rho" : 0.5, "crossSection" : FilletCrossSection.CONIC, "allowEdgeOverflow" : false});
        }
        {
            var Q0;
            Q0=makeQuery(id+"F34.opFillet","BLEND_EDGE",EDGE,{"blendedFrom":[makeQuery(id+"F30.opExtrude","CAP_EDGE",EDGE,{"disambiguationData":[OSD([sQuery(id+"F29.wireOp",EDGE,"E10")])],"isStart":true}),makeQuery(id+"F32.boolean.opBoolean","COPY",FACE,{"derivedFrom":makeQuery(id+"F32.opExtrude","SWEPT_FACE",FACE,{"disambiguationData":[OSD([sQuery(id+"F31.wireOp",EDGE,"E13")])]})})],"blendedInto":[makeQuery(id+"F32.boolean.opBoolean","COPY",FACE,{"derivedFrom":makeQuery(id+"F32.opExtrude","SWEPT_FACE",FACE,{"disambiguationData":[OSD([sQuery(id+"F31.wireOp",EDGE,"E13")])]})})]});
            var Q1;
            Q1=makeQuery(id+"F34.opFillet","BLEND_EDGE",EDGE,{"blendedFrom":[makeQuery(id+"F30.opExtrude","CAP_EDGE",EDGE,{"disambiguationData":[OSD([sQuery(id+"F29.wireOp",EDGE,"E11")])],"isStart":true}),makeQuery(id+"F32.boolean.opBoolean","COPY",FACE,{"derivedFrom":makeQuery(id+"F32.opExtrude","SWEPT_FACE",FACE,{"disambiguationData":[OSD([sQuery(id+"F31.wireOp",EDGE,"E13")])]})})],"blendedInto":[makeQuery(id+"F32.boolean.opBoolean","COPY",FACE,{"derivedFrom":makeQuery(id+"F32.opExtrude","SWEPT_FACE",FACE,{"disambiguationData":[OSD([sQuery(id+"F31.wireOp",EDGE,"E13")])]})})]});
            fillet(context, id + "F66", {"entities" : qUnion([Q0, Q1]), "radius" : 2.4 * mm, "tangentPropagation" : true, "allowEdgeOverflow" : false});
        }
    });
